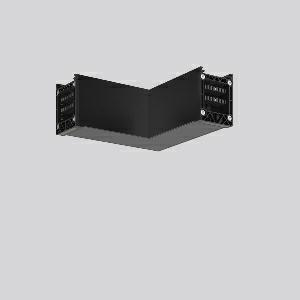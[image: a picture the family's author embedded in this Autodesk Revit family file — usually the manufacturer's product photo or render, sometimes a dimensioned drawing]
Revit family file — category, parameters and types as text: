
# Revit family: linedo_l-verbindung_982773_003_1_3b48
name_source: partatom
category: Lighting Fixtures
units: mm (PartAtom-declared; Revit-internal decimal feet)

## family parameters
Cut with Voids When Loaded = No
Host = Face
Light Source = No
Part Type = Normal
Room Calculation Point = No
Round Connector Dimension = Use Diameter
Shared = No

## types (1)
- LINEDO L-Verbindung
    Apparent Load = 0 VA
    Default Elevation = 1800 mm
    Description = Series: LINEDO
L-connector, 14-pole, connection socket / socket. Housing: extruded aluminium profile, powder-coated. Cover made of plastic, surface like housing. LINEDO plug system, plastic, black. Easy connection for rigid or flexible wires. 2 membrane cable entries (M25). Suitable for power supply in 7-pole version. Ready prewired. Colour-coded individual cables enable easy electromechanical separation.
Colour: jet black (RAL 9005)
Length: 185 mm
Width: 185 mm
Height: 76 mm
Weight: 730 g
    Height = 76 mm
    Lamp = 0 x
    Length = 185 mm
    Luminous efficacy = 0 lm/W
    Manufacturer = RZB
    ModVariant = No
    Model = 982773.003.1
    Mounting Place = Ceiling
    Mounting Type = Surface mounted
    Number of Poles = 1
    OnlyDefault = Yes
    Power Factor = 1
    Product Name = LINEDO L-Verbindung
    Product group = Continuous line luminaire system Linedo IP 54
    ProductGroupID = 314
    Protection Class = Protection class I
    Protection Degree = Degree of protection
    RLX_Detail_Level = 1
    RLX_Emergency_Light_Flux = 0 lm
    RLX_Emergency_Type = 0
    RLX_Emergency_Type_DB = No
    RlxData = <blob elided: 19017 chars, md5=94fa5399>
    Standby Power = 0 W
    System Light Flux = 0 lm
    System Power = 0 W
    Type Comments = Product without accessories
    Type Image = 982773.003.1.jpg
    URL = http://relux.com
    VarID = ---
    Voltage = 0 V
    Weight = 0.00 kg
    Width = 185 mm

## geometry (parser evidence)
native form markers: Blend x4, Sweep x11
no freeform markers — native parametric forms only
